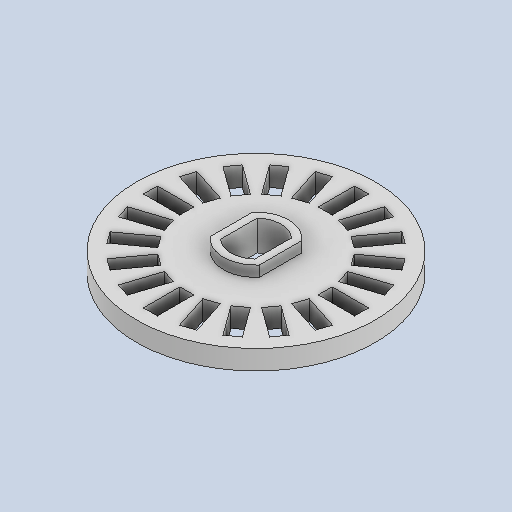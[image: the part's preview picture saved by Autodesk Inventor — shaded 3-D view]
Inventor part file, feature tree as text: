
AUTODESK INVENTOR PART (.ipt)
format: ipt  version: 2022 (Build 260153070, 153G)  size: 243,200 bytes
history: native  units: in
note: dims shown in document units (in); Inventor stores cm internally (conversion verified against a paired STEP export)
features: extrude x2, sketch x2
ambient origin geometry x8: Origin, YZ Plane, XZ Plane, XY Plane, X Axis, Y Axis, Z Axis, Center Point
bodies: Solid1 (feature_tree)
feature tree (4):
  extrude  "Extrusion1"  Depth=0.2126in
  extrude  "Extrusion2"  Depth=0.0453in
  sketch  "Sketch1"  dims[d0=1.0138in d1=0.2126in]
  sketch  "Sketch2"  dims[d3=0.1457in d4=0.187in d5=0.0591in d6=0.0591in d7=7.874in d9=360.0deg d11=0.0827in d12=0.0in d13=0.0315in d14=0.0315in d15=0.0315in d16=0.0453in d17=0.0in]
